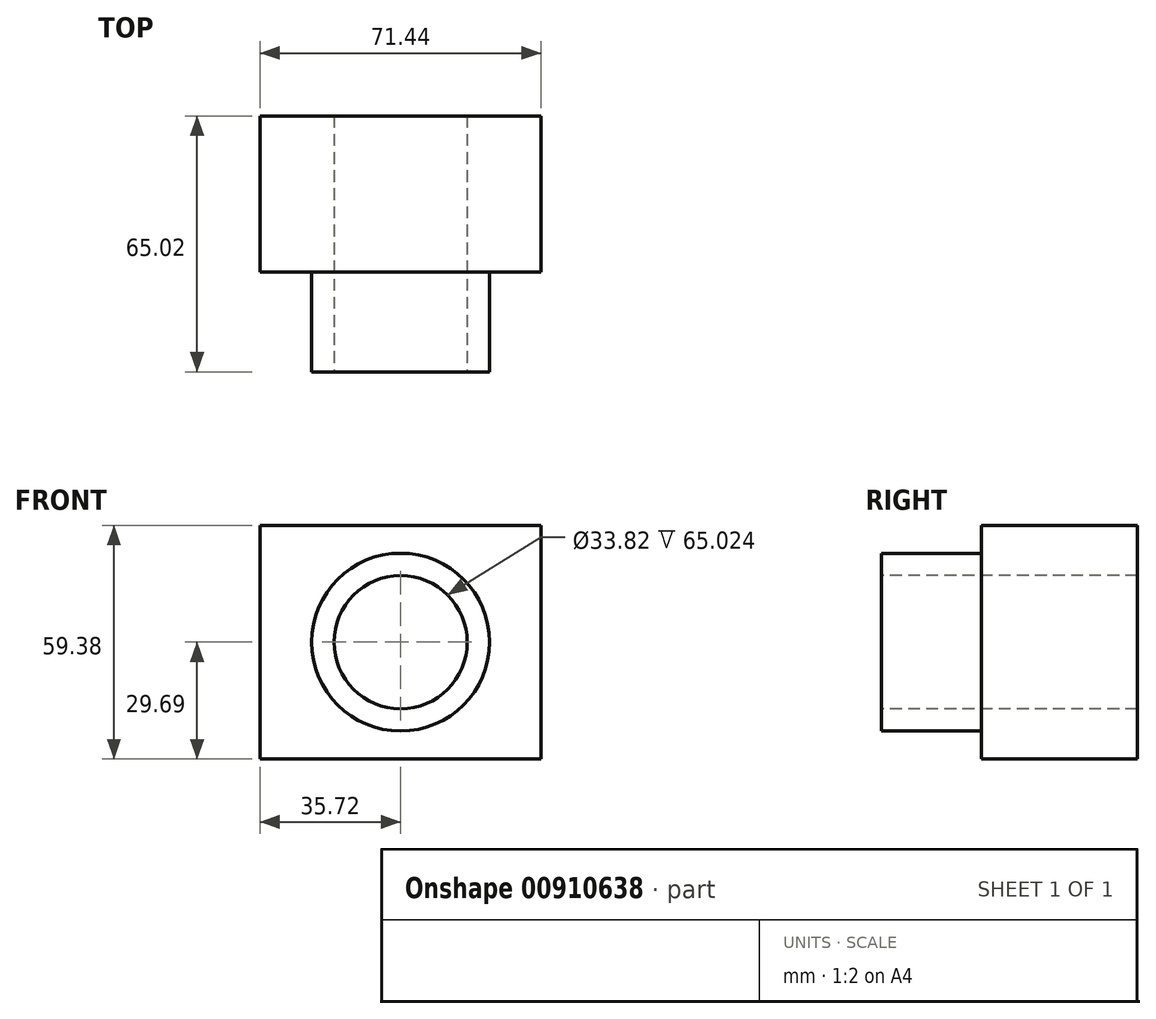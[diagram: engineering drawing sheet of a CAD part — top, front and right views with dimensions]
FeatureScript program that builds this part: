
annotation { "Feature Type Name" : "Feature", "Feature Type Description" : "" }
export const myFeature = defineFeature(function(context is Context, id is Id, definition is map)
    precondition{}
    {
        {
            var Q0;
            Q0=qCreatedBy(makeId("Front.planeOp"),FACE);
            var sketch = newSketch(context, id + "F0", { "sketchPlane" : qUnion([Q0])});
            skLineSegment(sketch, "E0.bottom", {"start": v(35.72, -29.7) * mm, "end": v(-35.72, -29.7) * mm});
            skLineSegment(sketch, "E0.top", {"start": v(35.72, 29.7) * mm, "end": v(-35.72, 29.7) * mm});
            skLineSegment(sketch, "E0.left", {"start": v(35.72, -29.7) * mm, "end": v(35.72, 29.7) * mm});
            skLineSegment(sketch, "E0.right", {"start": v(-35.72, -29.7) * mm, "end": v(-35.72, 29.7) * mm});
            skPoint(sketch, "E0.middle", {"position": v(0, 0) * mm});
            skSolve(sketch);
        }
        {
            var Q0;
            Q0=qSketchRegion(id+"F0",true);
            extrude(context, id + "F1", {"entities" : qUnion([Q0]), "depth" : 39.62 * mm});
        }
        {
            var Q0;
            Q0=makeQuery(id+"F1.opExtrude","CAP_FACE",FACE,{"disambiguationData":[OSD([sQuery(id+"F0.wireOp",EDGE,"E0.bottom"),sQuery(id+"F0.wireOp",EDGE,"E0.top"),sQuery(id+"F0.wireOp",EDGE,"E0.left"),sQuery(id+"F0.wireOp",EDGE,"E0.right")])],"isStart":false});
            var sketch = newSketch(context, id + "F2", { "sketchPlane" : qUnion([Q0])});
            skCircle(sketch, "E1", {"center": v(0, 0) * mm, "radius": 22.6 * mm});
            skSolve(sketch);
        }
        {
            var Q0;
            Q0=qSketchRegion(id+"F2",true);
            extrude(context, id + "F3", {"entities" : qUnion([Q0]), "operationType" : NewBodyOperationType.ADD, "depth" : 25.4 * mm});
        }
        {
            var Q0;
            Q0=makeQuery(id+"F3.opExtrude","CAP_FACE",FACE,{"disambiguationData":[OSD([sQuery(id+"F2.wireOp",EDGE,"E1")])],"isStart":false});
            var sketch = newSketch(context, id + "F4", { "sketchPlane" : qUnion([Q0])});
            skCircle(sketch, "E2", {"center": v(0, 0) * mm, "radius": 16.91 * mm});
            skSolve(sketch);
        }
        {
            var Q0;
            Q0=qSketchRegion(id+"F4",true);
            extrude(context, id + "F5", {"entities" : qUnion([Q0]), "operationType" : NewBodyOperationType.REMOVE, "endBound" : BoundingType.THROUGH_ALL, "oppositeDirection" : true, "depth" : 25.4 * mm});
        }
    });
